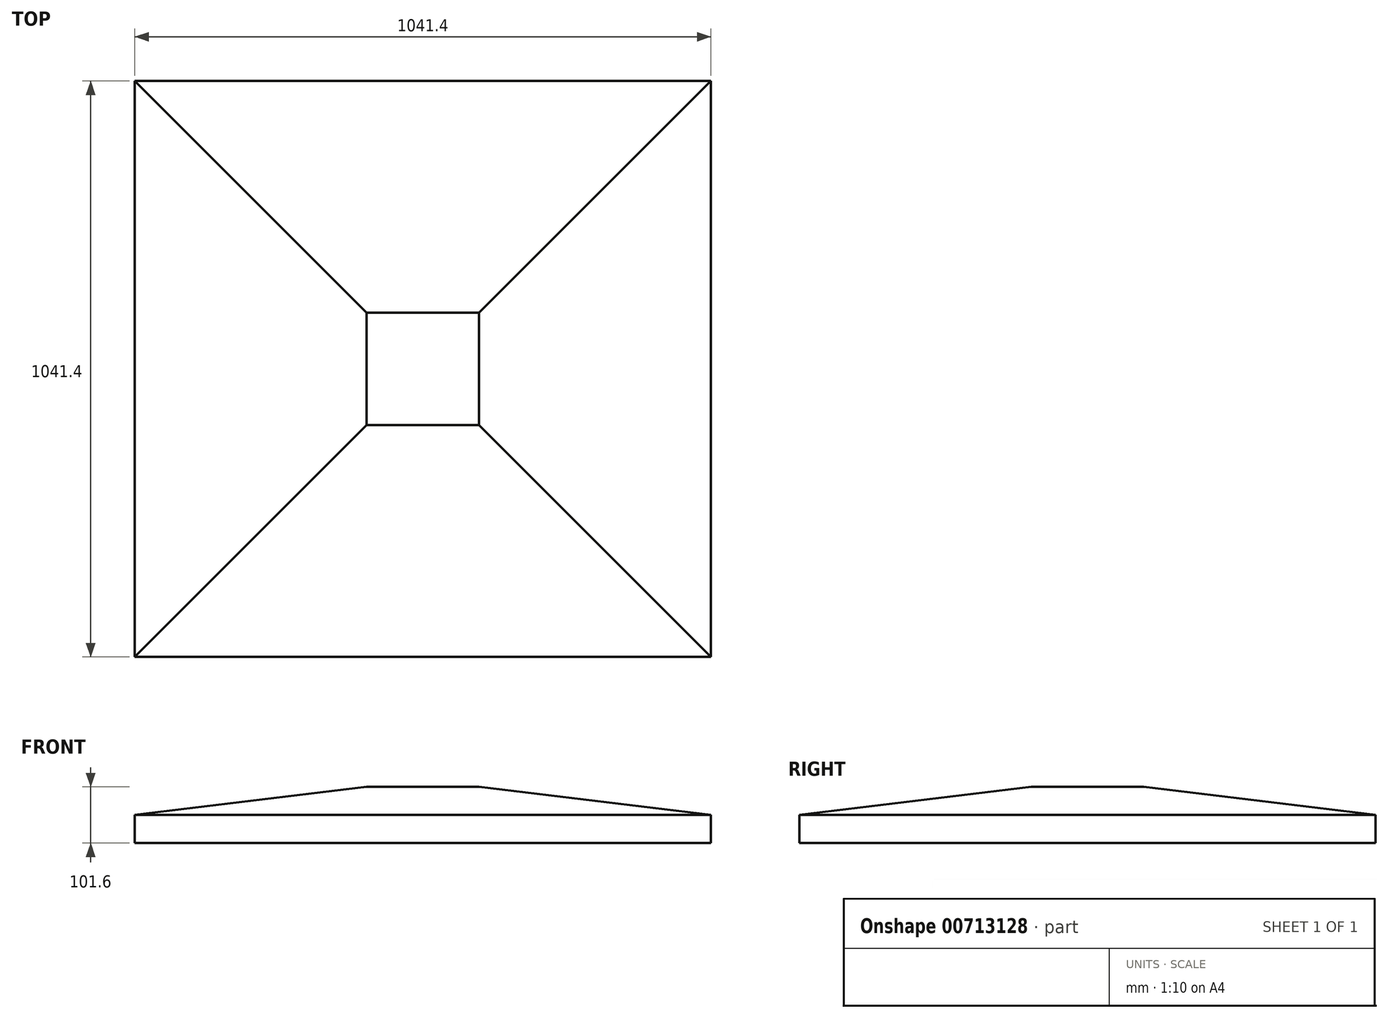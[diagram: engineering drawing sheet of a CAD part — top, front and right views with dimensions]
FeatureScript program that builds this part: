
annotation { "Feature Type Name" : "Feature", "Feature Type Description" : "" }
export const myFeature = defineFeature(function(context is Context, id is Id, definition is map)
    precondition{}
    {
        {
            var Q0;
            Q0=qCreatedBy(makeId("Top.planeOp"),FACE);
            var sketch = newSketch(context, id + "F0", { "sketchPlane" : qUnion([Q0])});
            skLineSegment(sketch, "E0.bottom", {"start": v(-520.7, -520.7) * mm, "end": v(520.7, -520.7) * mm});
            skLineSegment(sketch, "E0.top", {"start": v(-520.7, 520.7) * mm, "end": v(520.7, 520.7) * mm});
            skLineSegment(sketch, "E0.left", {"start": v(-520.7, -520.7) * mm, "end": v(-520.7, 520.7) * mm});
            skLineSegment(sketch, "E0.right", {"start": v(520.7, -520.7) * mm, "end": v(520.7, 520.7) * mm});
            skPoint(sketch, "E0.middle", {"position": v(0, 0) * mm});
            skSolve(sketch);
        }
        {
            var Q0;
            Q0 = qSketchRegion(id + "F0", true);
            extrude(context, id + "F1", {"entities" : qUnion([Q0]), "depth" : 50.8 * mm, "offsetDistance" : 25.4 * mm});
        }
        {
            var Q0;
            Q0=makeQuery(id+"F1.opExtrude","CAP_FACE",FACE,{"disambiguationData":[OSD([sQuery(id+"F0.wireOp",EDGE,"E0.bottom"),sQuery(id+"F0.wireOp",EDGE,"E0.top"),sQuery(id+"F0.wireOp",EDGE,"E0.left"),sQuery(id+"F0.wireOp",EDGE,"E0.right")])],"isStart":false});
            var sketch = newSketch(context, id + "F2", { "sketchPlane" : qUnion([Q0])});
            skSolve(sketch);
        }
        {
            var Q0;
            Q0=makeQuery(id+"F2.imprint","IMPRINT",FACE,{"disambiguationData":[TD([[makeQuery(id+"F2.imprint","IMPRINT",EDGE,{"derivedFrom":makeQuery(id+"F1.opExtrude","CAP_EDGE",EDGE,{"disambiguationData":[OSD([sQuery(id+"F0.wireOp",EDGE,"E0.bottom")])],"isStart":false})}),1.0]])]});
            cPlane(context, id + "F3", {"entities" : qUnion([Q0]), "cplaneType" : CPlaneType.OFFSET, "offset" : 50.8 * mm, "width" : 152.4 * mm, "height" : 152.4 * mm});
        }
        {
            var Q0;
            Q0=qCreatedBy(id+"F3.planeOp",FACE);
            var sketch = newSketch(context, id + "F4", { "sketchPlane" : qUnion([Q0])});
            skLineSegment(sketch, "E1.bottom", {"start": v(101.6, -101.6) * mm, "end": v(-101.6, -101.6) * mm});
            skLineSegment(sketch, "E1.top", {"start": v(101.6, 101.6) * mm, "end": v(-101.6, 101.6) * mm});
            skLineSegment(sketch, "E1.left", {"start": v(101.6, -101.6) * mm, "end": v(101.6, 101.6) * mm});
            skLineSegment(sketch, "E1.right", {"start": v(-101.6, -101.6) * mm, "end": v(-101.6, 101.6) * mm});
            skPoint(sketch, "E1.middle", {"position": v(0, 0) * mm});
            skSolve(sketch);
        }
        {
            var Q1;
            Q1=makeQuery(id+"F2.imprint","IMPRINT",FACE,{"disambiguationData":[TD([[makeQuery(id+"F2.imprint","IMPRINT",EDGE,{"derivedFrom":makeQuery(id+"F1.opExtrude","CAP_EDGE",EDGE,{"disambiguationData":[OSD([sQuery(id+"F0.wireOp",EDGE,"E0.bottom")])],"isStart":false})}),1.0]])]});
            var Q2;
            Q2=makeQuery(id+"F4.imprint","IMPRINT",FACE,{"disambiguationData":[TD([[makeQuery(id+"F4.imprint","IMPRINT",EDGE,{"derivedFrom":sQuery(id+"F4.wireOp",EDGE,"E1.bottom")}),-1.0]])]});
            loft(context, id + "F5", {"operationType" : NewBodyOperationType.ADD, "sheetProfilesArray" : [{ "sheetProfileEntities" : qUnion([Q1]) }, { "sheetProfileEntities" : qUnion([Q2]) }]});
        }
    });
